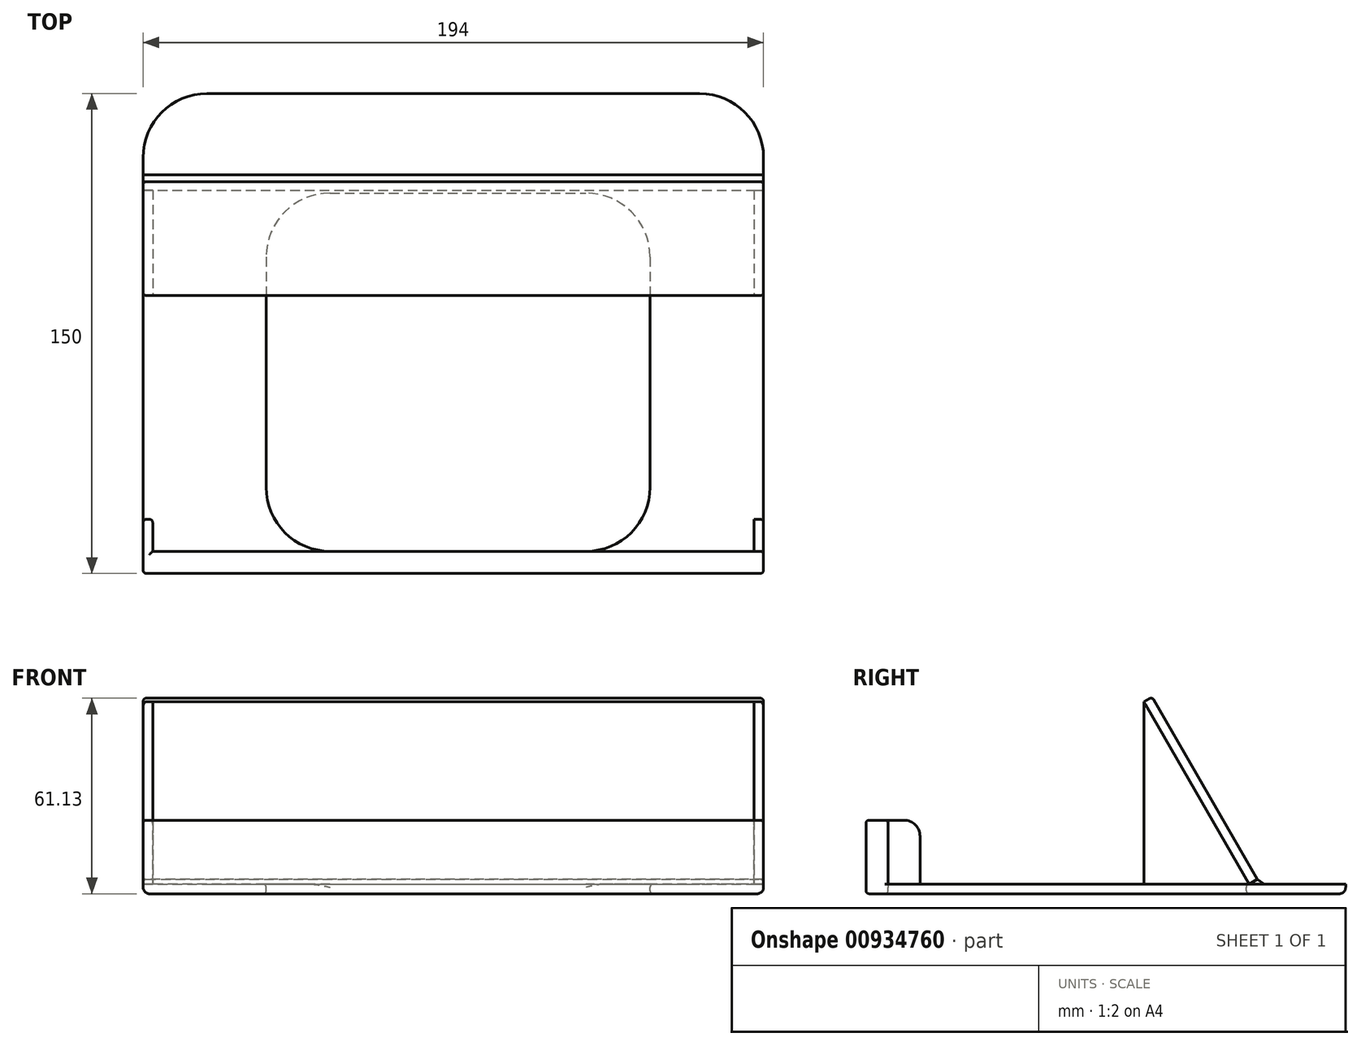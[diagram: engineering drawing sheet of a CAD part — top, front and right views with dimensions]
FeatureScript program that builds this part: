
annotation { "Feature Type Name" : "Feature", "Feature Type Description" : "" }
export const myFeature = defineFeature(function(context is Context, id is Id, definition is map)
    precondition{}
    {
        {
            var Q0;
            Q0=qCreatedBy(makeId("Top.planeOp"),FACE);
            var sketch = newSketch(context, id + "F0", { "sketchPlane" : qUnion([Q0])});
            skLineSegment(sketch, "E0.bottom", {"start": v(-88.92, 68) * mm, "end": v(105.08, 68) * mm});
            skLineSegment(sketch, "E0.top", {"start": v(-88.92, -82) * mm, "end": v(105.08, -82) * mm});
            skLineSegment(sketch, "E0.left", {"start": v(-88.92, 68) * mm, "end": v(-88.92, -82) * mm});
            skLineSegment(sketch, "E0.right", {"start": v(105.08, 68) * mm, "end": v(105.08, -82) * mm});
            skSolve(sketch);
        }
        {
            var Q0;
            Q0 = qSketchRegion(id + "F0", true);
            extrude(context, id + "F1", {"entities" : qUnion([Q0]), "depth" : 3 * mm, "offsetDistance" : 25 * mm});
        }
        {
            var Q0;
            Q0=makeQuery(id+"F1.opExtrude","SWEPT_FACE",FACE,{"disambiguationData":[OSD([sQuery(id+"F0.wireOp",EDGE,"E0.left")])]});
            var sketch = newSketch(context, id + "F2", { "sketchPlane" : qUnion([Q0])});
            skLineSegment(sketch, "E1.bottom", {"start": v(82, 3) * mm, "end": v(75.09, 3) * mm});
            skLineSegment(sketch, "E1.top", {"start": v(82, 23) * mm, "end": v(75.09, 23) * mm});
            skLineSegment(sketch, "E1.left", {"start": v(82, 3) * mm, "end": v(82, 23) * mm});
            skLineSegment(sketch, "E1.right", {"start": v(75.09, 3) * mm, "end": v(75.09, 23) * mm});
            skSolve(sketch);
        }
        {
            var Q0;
            Q0=makeQuery(id+"F2.imprint","IMPRINT",FACE,{"disambiguationData":[TD([[makeQuery(id+"F2.imprint","IMPRINT",EDGE,{"derivedFrom":sQuery(id+"F2.wireOp",EDGE,"E1.bottom")}),1.0]])]});
            extrude(context, id + "F3", {"entities" : qUnion([Q0]), "operationType" : NewBodyOperationType.ADD, "oppositeDirection" : true, "depth" : 194 * mm, "offsetDistance" : 25 * mm});
        }
        {
            var Q0;
            Q0=makeQuery(id+"F3.boolean.opBoolean","MERGE",FACE,{"derivedFrom":[makeQuery(id+"F1.opExtrude","SWEPT_FACE",FACE,{"disambiguationData":[OSD([sQuery(id+"F0.wireOp",EDGE,"E0.left")])]}),makeQuery(id+"F3.opExtrude","CAP_FACE",FACE,{"disambiguationData":[OSD([sQuery(id+"F2.wireOp",EDGE,"E1.bottom"),sQuery(id+"F2.wireOp",EDGE,"E1.top"),sQuery(id+"F2.wireOp",EDGE,"E1.left"),sQuery(id+"F2.wireOp",EDGE,"E1.right")])],"isStart":true})]});
            var sketch = newSketch(context, id + "F4", { "sketchPlane" : qUnion([Q0])});
            skLineSegment(sketch, "E2", {"start": v(-37.82, 3) * mm, "end": v(-4.91, 60) * mm});
            skLineSegment(sketch, "E3", {"start": v(-4.91, 60) * mm, "end": v(-4.91, 3) * mm});
            skLineSegment(sketch, "E4", {"start": v(-4.91, 3) * mm, "end": v(-37.82, 3) * mm});
            skSolve(sketch);
        }
        {
            var Q0;
            Q0 = qSketchRegion(id + "F4", true);
            extrude(context, id + "F5", {"entities" : qUnion([Q0]), "operationType" : NewBodyOperationType.ADD, "oppositeDirection" : true, "depth" : 3 * mm, "offsetDistance" : 25 * mm});
        }
        {
            var Q0;
            Q0=makeQuery(id+"F1.opExtrude","SWEPT_FACE",FACE,{"disambiguationData":[OSD([sQuery(id+"F0.wireOp",EDGE,"E0.right")])]});
            var sketch = newSketch(context, id + "F6", { "sketchPlane" : qUnion([Q0])});
            skLineSegment(sketch, "E5.0", {"start": v(37.82, 3) * mm, "end": v(4.91, 60) * mm});
            skPoint(sketch, "E6.0", {"position": v(4.91, 31.5) * mm});
            skLineSegment(sketch, "E7.0", {"start": v(4.91, 60) * mm, "end": v(4.91, 3) * mm});
            skLineSegment(sketch, "E8.0", {"start": v(37.82, 3) * mm, "end": v(4.91, 3) * mm});
            skSolve(sketch);
        }
        {
            var Q0;
            Q0=makeQuery(id+"F6.imprint","IMPRINT",FACE,{"disambiguationData":[TD([[makeQuery(id+"F6.imprint","IMPRINT",EDGE,{"derivedFrom":sQuery(id+"F6.wireOp",EDGE,"E5.0")}),1.0]])]});
            extrude(context, id + "F7", {"entities" : qUnion([Q0]), "oppositeDirection" : true, "depth" : 3 * mm, "offsetDistance" : 25 * mm});
        }
        {
            var Q0;
            Q0=makeQuery(id+"F7.opExtrude","SWEPT_FACE",FACE,{"disambiguationData":[OSD([sQuery(id+"F6.wireOp",EDGE,"E5.0")])]});
            var sketch = newSketch(context, id + "F8", { "sketchPlane" : qUnion([Q0])});
            skLineSegment(sketch, "E9.0", {"start": v(-105.08, -16.31) * mm, "end": v(-105.08, 49.5) * mm});
            skLineSegment(sketch, "E10.0", {"start": v(88.92, -16.31) * mm, "end": v(88.92, 49.5) * mm});
            skLineSegment(sketch, "E11", {"start": v(-105.08, 49.5) * mm, "end": v(88.92, 49.5) * mm});
            skLineSegment(sketch, "E12", {"start": v(-105.08, -16.31) * mm, "end": v(88.92, -16.31) * mm});
            skSolve(sketch);
        }
        {
            var Q0;
            Q0 = qSketchRegion(id + "F8", true);
            extrude(context, id + "F9", {"entities" : qUnion([Q0]), "depth" : 3 * mm, "offsetDistance" : 25 * mm});
        }
        {
            var Q0;
            Q0=makeQuery(id+"F9.opExtrude","SWEPT_FACE",FACE,{"disambiguationData":[OSD([sQuery(id+"F8.wireOp",EDGE,"E10.0")])]});
            var sketch = newSketch(context, id + "F10", { "sketchPlane" : qUnion([Q0])});
            skLineSegment(sketch, "E13.0", {"start": v(-40.42, 4.5) * mm, "end": v(-37.82, 3) * mm});
            skLineSegment(sketch, "E14.0", {"start": v(-68, 3) * mm, "end": v(-37.82, 3) * mm});
            skLineSegment(sketch, "E15", {"start": v(-40.42, 4.5) * mm, "end": v(-42.55, 3) * mm});
            skLineSegment(sketch, "E16", {"start": v(-42.55, 3) * mm, "end": v(-37.82, 3) * mm});
            skSolve(sketch);
        }
        {
            var Q0;
            Q0=makeQuery(id+"F10.imprint","IMPRINT",FACE,{"disambiguationData":[TD([[makeQuery(id+"F10.imprint","IMPRINT",EDGE,{"derivedFrom":sQuery(id+"F10.wireOp",EDGE,"E13.0")}),-1.0]])]});
            extrude(context, id + "F11", {"entities" : qUnion([Q0]), "oppositeDirection" : true, "depth" : 194 * mm, "offsetDistance" : 25 * mm});
        }
        {
            var Q0;
            Q0=makeQuery(id+"F5.boolean.opBoolean","MERGE",FACE,{"derivedFrom":[makeQuery(id+"F3.boolean.opBoolean","MERGE",FACE,{"derivedFrom":[makeQuery(id+"F1.opExtrude","SWEPT_FACE",FACE,{"disambiguationData":[OSD([sQuery(id+"F0.wireOp",EDGE,"E0.left")])]}),makeQuery(id+"F3.opExtrude","CAP_FACE",FACE,{"disambiguationData":[OSD([sQuery(id+"F2.wireOp",EDGE,"E1.bottom"),sQuery(id+"F2.wireOp",EDGE,"E1.top"),sQuery(id+"F2.wireOp",EDGE,"E1.left"),sQuery(id+"F2.wireOp",EDGE,"E1.right")])],"isStart":true})]}),makeQuery(id+"F5.opExtrude","CAP_FACE",FACE,{"disambiguationData":[OSD([sQuery(id+"F4.wireOp",EDGE,"E2"),sQuery(id+"F4.wireOp",EDGE,"E3"),sQuery(id+"F4.wireOp",EDGE,"E4")])],"isStart":true})]});
            var sketch = newSketch(context, id + "F12", { "sketchPlane" : qUnion([Q0])});
            skLineSegment(sketch, "E17.bottom", {"start": v(75.09, 23) * mm, "end": v(65.09, 23) * mm});
            skLineSegment(sketch, "E17.top", {"start": v(75.09, 3) * mm, "end": v(65.09, 3) * mm});
            skLineSegment(sketch, "E17.left", {"start": v(75.09, 23) * mm, "end": v(75.09, 3) * mm});
            skLineSegment(sketch, "E17.right", {"start": v(65.09, 23) * mm, "end": v(65.09, 3) * mm});
            skSolve(sketch);
        }
        {
            var Q0;
            Q0 = qSketchRegion(id + "F12", true);
            extrude(context, id + "F13", {"entities" : qUnion([Q0]), "operationType" : NewBodyOperationType.ADD, "oppositeDirection" : true, "depth" : 3 * mm, "offsetDistance" : 25 * mm});
        }
        {
            var Q0;
            Q0=makeQuery(id+"F13.opExtrude","SWEPT_EDGE",EDGE,{"disambiguationData":[OSD([sQuery(id+"F12.wireOp",EDGE,"E17.bottom"),sQuery(id+"F12.wireOp",EDGE,"E17.right")])]});
            fillet(context, id + "F14", {"entities" : qUnion([Q0]), "radius" : 5 * mm, "tangentPropagation" : true, "allowEdgeOverflow" : false});
        }
        {
            var Q0;
            Q0=makeQuery(id+"F9.opExtrude","CAP_EDGE",EDGE,{"disambiguationData":[OSD([sQuery(id+"F8.wireOp",EDGE,"E11")])],"isStart":false});
            fillet(context, id + "F15", {"entities" : qUnion([Q0]), "radius" : 1 * mm, "tangentPropagation" : true, "allowEdgeOverflow" : false});
        }
        {
            var Q0;
            Q0=makeQuery(id+"F9.opExtrude","CAP_EDGE",EDGE,{"disambiguationData":[OSD([sQuery(id+"F8.wireOp",EDGE,"E10.0")])],"isStart":false});
            fillet(context, id + "F16", {"entities" : qUnion([Q0]), "radius" : 1 * mm, "tangentPropagation" : true, "allowEdgeOverflow" : false});
        }
        {
            var Q0;
            Q0=makeQuery(id+"F3.boolean.opBoolean","MERGE",FACE,{"derivedFrom":[makeQuery(id+"F1.opExtrude","SWEPT_FACE",FACE,{"disambiguationData":[OSD([sQuery(id+"F0.wireOp",EDGE,"E0.right")])]}),makeQuery(id+"F3.opExtrude","CAP_FACE",FACE,{"disambiguationData":[OSD([sQuery(id+"F2.wireOp",EDGE,"E1.bottom"),sQuery(id+"F2.wireOp",EDGE,"E1.top"),sQuery(id+"F2.wireOp",EDGE,"E1.left"),sQuery(id+"F2.wireOp",EDGE,"E1.right")])],"isStart":false})]});
            var sketch = newSketch(context, id + "F17", { "sketchPlane" : qUnion([Q0])});
            skPoint(sketch, "E18.0", {"position": v(-72.59, 23) * mm});
            skArc(sketch, "E19.0", {"start": v(-65.09, 18) * mm, "mid": v(-66.55, 21.54) * mm, "end": v(-70.09, 23) * mm});
            skLineSegment(sketch, "E20.0", {"start": v(-65.09, 18) * mm, "end": v(-65.09, 3) * mm});
            skLineSegment(sketch, "E21.0.0", {"start": v(-65.09, 3) * mm, "end": v(-65.09, 18) * mm});
            skLineSegment(sketch, "E21.0.2", {"start": v(-70.09, 23) * mm, "end": v(-75.09, 23) * mm});
            skLineSegment(sketch, "E21.0.3", {"start": v(-75.09, 23) * mm, "end": v(-75.09, 3) * mm});
            skLineSegment(sketch, "E21.0.4", {"start": v(-75.09, 3) * mm, "end": v(-65.09, 3) * mm});
            skSolve(sketch);
        }
        {
            var Q0;
            Q0 = qSketchRegion(id + "F17", true);
            extrude(context, id + "F18", {"entities" : qUnion([Q0]), "oppositeDirection" : true, "depth" : 3 * mm, "offsetDistance" : 25 * mm});
        }
        {
            var Q0;
            Q0=makeQuery(id+"F9.opExtrude","CAP_EDGE",EDGE,{"disambiguationData":[OSD([sQuery(id+"F8.wireOp",EDGE,"E9.0")])],"isStart":false});
            fillet(context, id + "F19", {"entities" : qUnion([Q0]), "radius" : 1 * mm, "tangentPropagation" : true, "allowEdgeOverflow" : false});
        }
        {
            var Q0;
            Q0=makeQuery(id+"F7.opExtrude","CAP_EDGE",EDGE,{"disambiguationData":[OSD([sQuery(id+"F6.wireOp",EDGE,"E7.0")])],"isStart":true});
            fillet(context, id + "F20", {"entities" : qUnion([Q0]), "radius" : 1 * mm, "tangentPropagation" : true, "allowEdgeOverflow" : false});
        }
        {
            var Q0;
            Q0=makeQuery(id+"F3.opExtrude","SWEPT_EDGE",EDGE,{"disambiguationData":[OSD([sQuery(id+"F2.wireOp",EDGE,"E1.top"),sQuery(id+"F2.wireOp",EDGE,"E1.left")])]});
            fillet(context, id + "F21", {"entities" : qUnion([Q0]), "radius" : 1 * mm, "tangentPropagation" : true, "allowEdgeOverflow" : false});
        }
        {
            var Q0;
            Q0=makeQuery(id+"F1.opExtrude","CAP_FACE",FACE,{"disambiguationData":[OSD([sQuery(id+"F0.wireOp",EDGE,"E0.bottom"),sQuery(id+"F0.wireOp",EDGE,"E0.top"),sQuery(id+"F0.wireOp",EDGE,"E0.left"),sQuery(id+"F0.wireOp",EDGE,"E0.right")])],"isStart":false});
            var sketch = newSketch(context, id + "F22", { "sketchPlane" : qUnion([Q0])});
            skPoint(sketch, "E22", {"position": v(9.58, -75.09) * mm});
            skLineSegment(sketch, "E23.bottom", {"start": v(-50.42, 36.91) * mm, "end": v(69.58, 36.91) * mm});
            skLineSegment(sketch, "E23.top", {"start": v(-50.42, -75.09) * mm, "end": v(69.58, -75.09) * mm});
            skLineSegment(sketch, "E23.left", {"start": v(-50.42, 36.91) * mm, "end": v(-50.42, -75.09) * mm});
            skLineSegment(sketch, "E23.right", {"start": v(69.58, 36.91) * mm, "end": v(69.58, -75.09) * mm});
            skSolve(sketch);
        }
        {
            var Q0;
            Q0 = qSketchRegion(id + "F22", true);
            extrude(context, id + "F23", {"entities" : qUnion([Q0]), "operationType" : NewBodyOperationType.REMOVE, "endBound" : BoundingType.THROUGH_ALL, "oppositeDirection" : true, "depth" : 25 * mm, "offsetDistance" : 25 * mm});
        }
        {
            var Q0;
            Q0=makeQuery(id+"F1.opExtrude","SWEPT_EDGE",EDGE,{"disambiguationData":[OSD([sQuery(id+"F0.wireOp",EDGE,"E0.bottom"),sQuery(id+"F0.wireOp",EDGE,"E0.left")])]});
            var Q1;
            Q1=makeQuery(id+"F1.opExtrude","SWEPT_EDGE",EDGE,{"disambiguationData":[OSD([sQuery(id+"F0.wireOp",EDGE,"E0.bottom"),sQuery(id+"F0.wireOp",EDGE,"E0.right")])]});
            var Q2;
            Q2=makeQuery(id+"F23.boolean.opBoolean","COPY",EDGE,{"derivedFrom":makeQuery(id+"F23.opExtrude","SWEPT_EDGE",EDGE,{"disambiguationData":[OSD([sQuery(id+"F22.wireOp",EDGE,"E23.bottom"),sQuery(id+"F22.wireOp",EDGE,"E23.right")])]})});
            var Q3;
            Q3=makeQuery(id+"F23.boolean.opBoolean","COPY",EDGE,{"derivedFrom":makeQuery(id+"F23.opExtrude","SWEPT_EDGE",EDGE,{"disambiguationData":[OSD([sQuery(id+"F22.wireOp",EDGE,"E23.bottom"),sQuery(id+"F22.wireOp",EDGE,"E23.left")])]})});
            fillet(context, id + "F24", {"entities" : qUnion([Q0, Q1, Q2, Q3]), "radius" : 20 * mm, "tangentPropagation" : true, "allowEdgeOverflow" : false});
        }
        {
            var Q0;
            Q0=makeQuery(id+"F23.boolean.opBoolean","COPY",EDGE,{"derivedFrom":makeQuery(id+"F23.opExtrude","SWEPT_EDGE",EDGE,{"disambiguationData":[OSD([sQuery(id+"F0.wireOp",EDGE,"E0.left"),sQuery(id+"F2.wireOp",EDGE,"E1.bottom"),sQuery(id+"F2.wireOp",EDGE,"E1.right"),sQuery(id+"F22.wireOp",EDGE,"E23.top"),sQuery(id+"F22.wireOp",EDGE,"E23.right")])]})});
            var Q1;
            Q1=makeQuery(id+"F23.boolean.opBoolean","COPY",EDGE,{"derivedFrom":makeQuery(id+"F23.opExtrude","SWEPT_EDGE",EDGE,{"disambiguationData":[OSD([sQuery(id+"F0.wireOp",EDGE,"E0.left"),sQuery(id+"F2.wireOp",EDGE,"E1.bottom"),sQuery(id+"F2.wireOp",EDGE,"E1.right"),sQuery(id+"F22.wireOp",EDGE,"E23.top"),sQuery(id+"F22.wireOp",EDGE,"E23.left")])]})});
            fillet(context, id + "F25", {"entities" : qUnion([Q0, Q1]), "radius" : 20 * mm, "tangentPropagation" : true, "allowEdgeOverflow" : false});
        }
        {
            var Q0;
            Q0=makeQuery(id+"F1.opExtrude","CAP_EDGE",EDGE,{"disambiguationData":[OSD([sQuery(id+"F0.wireOp",EDGE,"E0.left")])],"isStart":true});
            fillet(context, id + "F26", {"entities" : qUnion([Q0]), "radius" : 2 * mm, "tangentPropagation" : true, "allowEdgeOverflow" : false});
        }
        {
            var Q0;
            Q0=makeQuery(id+"F5.opExtrude","CAP_EDGE",EDGE,{"disambiguationData":[OSD([sQuery(id+"F4.wireOp",EDGE,"E3")])],"isStart":true});
            fillet(context, id + "F27", {"entities" : qUnion([Q0]), "radius" : 1 * mm, "tangentPropagation" : true, "allowEdgeOverflow" : false});
        }
        {
            var Q0;
            Q0=makeQuery(id+"F3.boolean.opBoolean","MERGE",FACE,{"derivedFrom":[makeQuery(id+"F1.opExtrude","SWEPT_FACE",FACE,{"disambiguationData":[OSD([sQuery(id+"F0.wireOp",EDGE,"E0.top")])]}),makeQuery(id+"F3.opExtrude","SWEPT_FACE",FACE,{"disambiguationData":[OSD([sQuery(id+"F2.wireOp",EDGE,"E1.left")])]})]});
            fillet(context, id + "F28", {"entities" : qUnion([Q0]), "radius" : 1 * mm, "tangentPropagation" : true, "allowEdgeOverflow" : false});
        }
        {
            var Q0;
            {var subQ0=sQuery(id+"F0.wireOp",EDGE,"E0.left");Q0=makeQuery(id+"F25.opFillet","BLEND_EDGE",EDGE,{"blendedFrom":[makeQuery(id+"F23.boolean.opBoolean","COPY",EDGE,{"derivedFrom":makeQuery(id+"F23.opExtrude","SWEPT_EDGE",EDGE,{"disambiguationData":[OSD([subQ0,sQuery(id+"F2.wireOp",EDGE,"E1.bottom"),sQuery(id+"F2.wireOp",EDGE,"E1.right"),sQuery(id+"F22.wireOp",EDGE,"E23.top"),sQuery(id+"F22.wireOp",EDGE,"E23.left")])]})}),makeQuery(id+"F1.opExtrude","CAP_FACE",FACE,{"disambiguationData":[OSD([sQuery(id+"F0.wireOp",EDGE,"E0.bottom"),sQuery(id+"F0.wireOp",EDGE,"E0.top"),subQ0,sQuery(id+"F0.wireOp",EDGE,"E0.right")])],"isStart":true})],"blendedInto":[makeQuery(id+"F1.opExtrude","CAP_FACE",FACE,{"disambiguationData":[OSD([sQuery(id+"F0.wireOp",EDGE,"E0.bottom"),sQuery(id+"F0.wireOp",EDGE,"E0.top"),subQ0,sQuery(id+"F0.wireOp",EDGE,"E0.right")])],"isStart":true})]});}
            var Q1;
            {var subQ0=sQuery(id+"F0.wireOp",EDGE,"E0.left");Q1=makeQuery(id+"F25.opFillet","BLEND_EDGE",EDGE,{"blendedFrom":[makeQuery(id+"F23.boolean.opBoolean","COPY",EDGE,{"derivedFrom":makeQuery(id+"F23.opExtrude","SWEPT_EDGE",EDGE,{"disambiguationData":[OSD([subQ0,sQuery(id+"F2.wireOp",EDGE,"E1.bottom"),sQuery(id+"F2.wireOp",EDGE,"E1.right"),sQuery(id+"F22.wireOp",EDGE,"E23.top"),sQuery(id+"F22.wireOp",EDGE,"E23.right")])]})}),makeQuery(id+"F1.opExtrude","CAP_FACE",FACE,{"disambiguationData":[OSD([sQuery(id+"F0.wireOp",EDGE,"E0.bottom"),sQuery(id+"F0.wireOp",EDGE,"E0.top"),subQ0,sQuery(id+"F0.wireOp",EDGE,"E0.right")])],"isStart":true})],"blendedInto":[makeQuery(id+"F1.opExtrude","CAP_FACE",FACE,{"disambiguationData":[OSD([sQuery(id+"F0.wireOp",EDGE,"E0.bottom"),sQuery(id+"F0.wireOp",EDGE,"E0.top"),subQ0,sQuery(id+"F0.wireOp",EDGE,"E0.right")])],"isStart":true})]});}
            var Q2;
            Q2=makeQuery(id+"F23.boolean.opBoolean","INTERSECT",EDGE,{"derivedFrom":[makeQuery(id+"F1.opExtrude","CAP_FACE",FACE,{"disambiguationData":[OSD([sQuery(id+"F0.wireOp",EDGE,"E0.bottom"),sQuery(id+"F0.wireOp",EDGE,"E0.top"),sQuery(id+"F0.wireOp",EDGE,"E0.left"),sQuery(id+"F0.wireOp",EDGE,"E0.right")])],"isStart":true}),makeQuery(id+"F23.opExtrude","SWEPT_FACE",FACE,{"disambiguationData":[OSD([sQuery(id+"F22.wireOp",EDGE,"E23.top")])]})]});
            var Q3;
            Q3=makeQuery(id+"F24.opFillet","BLEND_EDGE",EDGE,{"blendedFrom":[makeQuery(id+"F23.boolean.opBoolean","COPY",EDGE,{"derivedFrom":makeQuery(id+"F23.opExtrude","SWEPT_EDGE",EDGE,{"disambiguationData":[OSD([sQuery(id+"F22.wireOp",EDGE,"E23.bottom"),sQuery(id+"F22.wireOp",EDGE,"E23.right")])]})}),makeQuery(id+"F1.opExtrude","CAP_FACE",FACE,{"disambiguationData":[OSD([sQuery(id+"F0.wireOp",EDGE,"E0.bottom"),sQuery(id+"F0.wireOp",EDGE,"E0.top"),sQuery(id+"F0.wireOp",EDGE,"E0.left"),sQuery(id+"F0.wireOp",EDGE,"E0.right")])],"isStart":true})],"blendedInto":[makeQuery(id+"F1.opExtrude","CAP_FACE",FACE,{"disambiguationData":[OSD([sQuery(id+"F0.wireOp",EDGE,"E0.bottom"),sQuery(id+"F0.wireOp",EDGE,"E0.top"),sQuery(id+"F0.wireOp",EDGE,"E0.left"),sQuery(id+"F0.wireOp",EDGE,"E0.right")])],"isStart":true})]});
            var Q4;
            Q4=makeQuery(id+"F23.boolean.opBoolean","INTERSECT",EDGE,{"derivedFrom":[makeQuery(id+"F1.opExtrude","CAP_FACE",FACE,{"disambiguationData":[OSD([sQuery(id+"F0.wireOp",EDGE,"E0.bottom"),sQuery(id+"F0.wireOp",EDGE,"E0.top"),sQuery(id+"F0.wireOp",EDGE,"E0.left"),sQuery(id+"F0.wireOp",EDGE,"E0.right")])],"isStart":true}),makeQuery(id+"F23.opExtrude","SWEPT_FACE",FACE,{"disambiguationData":[OSD([sQuery(id+"F22.wireOp",EDGE,"E23.right")])]})]});
            var Q5;
            Q5=makeQuery(id+"F23.boolean.opBoolean","INTERSECT",EDGE,{"derivedFrom":[makeQuery(id+"F1.opExtrude","CAP_FACE",FACE,{"disambiguationData":[OSD([sQuery(id+"F0.wireOp",EDGE,"E0.bottom"),sQuery(id+"F0.wireOp",EDGE,"E0.top"),sQuery(id+"F0.wireOp",EDGE,"E0.left"),sQuery(id+"F0.wireOp",EDGE,"E0.right")])],"isStart":true}),makeQuery(id+"F23.opExtrude","SWEPT_FACE",FACE,{"disambiguationData":[OSD([sQuery(id+"F22.wireOp",EDGE,"E23.bottom")])]})]});
            var Q6;
            Q6=makeQuery(id+"F24.opFillet","BLEND_EDGE",EDGE,{"blendedFrom":[makeQuery(id+"F23.boolean.opBoolean","COPY",EDGE,{"derivedFrom":makeQuery(id+"F23.opExtrude","SWEPT_EDGE",EDGE,{"disambiguationData":[OSD([sQuery(id+"F22.wireOp",EDGE,"E23.bottom"),sQuery(id+"F22.wireOp",EDGE,"E23.left")])]})}),makeQuery(id+"F1.opExtrude","CAP_FACE",FACE,{"disambiguationData":[OSD([sQuery(id+"F0.wireOp",EDGE,"E0.bottom"),sQuery(id+"F0.wireOp",EDGE,"E0.top"),sQuery(id+"F0.wireOp",EDGE,"E0.left"),sQuery(id+"F0.wireOp",EDGE,"E0.right")])],"isStart":true})],"blendedInto":[makeQuery(id+"F1.opExtrude","CAP_FACE",FACE,{"disambiguationData":[OSD([sQuery(id+"F0.wireOp",EDGE,"E0.bottom"),sQuery(id+"F0.wireOp",EDGE,"E0.top"),sQuery(id+"F0.wireOp",EDGE,"E0.left"),sQuery(id+"F0.wireOp",EDGE,"E0.right")])],"isStart":true})]});
            var Q7;
            Q7=makeQuery(id+"F23.boolean.opBoolean","INTERSECT",EDGE,{"derivedFrom":[makeQuery(id+"F1.opExtrude","CAP_FACE",FACE,{"disambiguationData":[OSD([sQuery(id+"F0.wireOp",EDGE,"E0.bottom"),sQuery(id+"F0.wireOp",EDGE,"E0.top"),sQuery(id+"F0.wireOp",EDGE,"E0.left"),sQuery(id+"F0.wireOp",EDGE,"E0.right")])],"isStart":true}),makeQuery(id+"F23.opExtrude","SWEPT_FACE",FACE,{"disambiguationData":[OSD([sQuery(id+"F22.wireOp",EDGE,"E23.left")])]})]});
            fillet(context, id + "F29", {"entities" : qUnion([Q0, Q1, Q2, Q3, Q4, Q5, Q6, Q7]), "radius" : 1 * mm, "tangentPropagation" : true, "allowEdgeOverflow" : false});
        }
        {
            var Q0;
            Q0=makeQuery(id+"F24.opFillet","BLEND_EDGE",EDGE,{"blendedFrom":[makeQuery(id+"F23.boolean.opBoolean","COPY",EDGE,{"derivedFrom":makeQuery(id+"F23.opExtrude","SWEPT_EDGE",EDGE,{"disambiguationData":[OSD([sQuery(id+"F22.wireOp",EDGE,"E23.bottom"),sQuery(id+"F22.wireOp",EDGE,"E23.left")])]})}),makeQuery(id+"F1.opExtrude","CAP_FACE",FACE,{"disambiguationData":[OSD([sQuery(id+"F0.wireOp",EDGE,"E0.bottom"),sQuery(id+"F0.wireOp",EDGE,"E0.top"),sQuery(id+"F0.wireOp",EDGE,"E0.left"),sQuery(id+"F0.wireOp",EDGE,"E0.right")])],"isStart":false})],"blendedInto":[makeQuery(id+"F1.opExtrude","CAP_FACE",FACE,{"disambiguationData":[OSD([sQuery(id+"F0.wireOp",EDGE,"E0.bottom"),sQuery(id+"F0.wireOp",EDGE,"E0.top"),sQuery(id+"F0.wireOp",EDGE,"E0.left"),sQuery(id+"F0.wireOp",EDGE,"E0.right")])],"isStart":false})]});
            var Q1;
            Q1=makeQuery(id+"F23.boolean.opBoolean","COPY",EDGE,{"derivedFrom":makeQuery(id+"F23.opExtrude","CAP_EDGE",EDGE,{"disambiguationData":[OSD([sQuery(id+"F22.wireOp",EDGE,"E23.left")])],"isStart":true})});
            var Q2;
            Q2=makeQuery(id+"F24.opFillet","BLEND_EDGE",EDGE,{"blendedFrom":[makeQuery(id+"F23.boolean.opBoolean","COPY",EDGE,{"derivedFrom":makeQuery(id+"F23.opExtrude","SWEPT_EDGE",EDGE,{"disambiguationData":[OSD([sQuery(id+"F22.wireOp",EDGE,"E23.bottom"),sQuery(id+"F22.wireOp",EDGE,"E23.right")])]})}),makeQuery(id+"F1.opExtrude","CAP_FACE",FACE,{"disambiguationData":[OSD([sQuery(id+"F0.wireOp",EDGE,"E0.bottom"),sQuery(id+"F0.wireOp",EDGE,"E0.top"),sQuery(id+"F0.wireOp",EDGE,"E0.left"),sQuery(id+"F0.wireOp",EDGE,"E0.right")])],"isStart":false})],"blendedInto":[makeQuery(id+"F1.opExtrude","CAP_FACE",FACE,{"disambiguationData":[OSD([sQuery(id+"F0.wireOp",EDGE,"E0.bottom"),sQuery(id+"F0.wireOp",EDGE,"E0.top"),sQuery(id+"F0.wireOp",EDGE,"E0.left"),sQuery(id+"F0.wireOp",EDGE,"E0.right")])],"isStart":false})]});
            var Q3;
            Q3=makeQuery(id+"F23.boolean.opBoolean","COPY",EDGE,{"derivedFrom":makeQuery(id+"F23.opExtrude","CAP_EDGE",EDGE,{"disambiguationData":[OSD([sQuery(id+"F22.wireOp",EDGE,"E23.right")])],"isStart":true})});
            var Q4;
            {var subQ0=sQuery(id+"F0.wireOp",EDGE,"E0.left");Q4=makeQuery(id+"F25.opFillet","BLEND_EDGE",EDGE,{"blendedFrom":[makeQuery(id+"F23.boolean.opBoolean","COPY",EDGE,{"derivedFrom":makeQuery(id+"F23.opExtrude","SWEPT_EDGE",EDGE,{"disambiguationData":[OSD([subQ0,sQuery(id+"F2.wireOp",EDGE,"E1.bottom"),sQuery(id+"F2.wireOp",EDGE,"E1.right"),sQuery(id+"F22.wireOp",EDGE,"E23.top"),sQuery(id+"F22.wireOp",EDGE,"E23.right")])]})}),makeQuery(id+"F1.opExtrude","CAP_FACE",FACE,{"disambiguationData":[OSD([sQuery(id+"F0.wireOp",EDGE,"E0.bottom"),sQuery(id+"F0.wireOp",EDGE,"E0.top"),subQ0,sQuery(id+"F0.wireOp",EDGE,"E0.right")])],"isStart":false})],"blendedInto":[makeQuery(id+"F1.opExtrude","CAP_FACE",FACE,{"disambiguationData":[OSD([sQuery(id+"F0.wireOp",EDGE,"E0.bottom"),sQuery(id+"F0.wireOp",EDGE,"E0.top"),subQ0,sQuery(id+"F0.wireOp",EDGE,"E0.right")])],"isStart":false})]});}
            var Q5;
            {var subQ0=sQuery(id+"F0.wireOp",EDGE,"E0.left");Q5=makeQuery(id+"F25.opFillet","BLEND_EDGE",EDGE,{"blendedFrom":[makeQuery(id+"F23.boolean.opBoolean","COPY",EDGE,{"derivedFrom":makeQuery(id+"F23.opExtrude","SWEPT_EDGE",EDGE,{"disambiguationData":[OSD([subQ0,sQuery(id+"F2.wireOp",EDGE,"E1.bottom"),sQuery(id+"F2.wireOp",EDGE,"E1.right"),sQuery(id+"F22.wireOp",EDGE,"E23.top"),sQuery(id+"F22.wireOp",EDGE,"E23.left")])]})}),makeQuery(id+"F1.opExtrude","CAP_FACE",FACE,{"disambiguationData":[OSD([sQuery(id+"F0.wireOp",EDGE,"E0.bottom"),sQuery(id+"F0.wireOp",EDGE,"E0.top"),subQ0,sQuery(id+"F0.wireOp",EDGE,"E0.right")])],"isStart":false})],"blendedInto":[makeQuery(id+"F1.opExtrude","CAP_FACE",FACE,{"disambiguationData":[OSD([sQuery(id+"F0.wireOp",EDGE,"E0.bottom"),sQuery(id+"F0.wireOp",EDGE,"E0.top"),subQ0,sQuery(id+"F0.wireOp",EDGE,"E0.right")])],"isStart":false})]});}
            fillet(context, id + "F30", {"entities" : qUnion([Q0, Q1, Q2, Q3, Q4, Q5]), "radius" : 1 * mm, "tangentPropagation" : true, "allowEdgeOverflow" : false});
        }
        {
            var Q0;
            Q0=makeQuery(id+"F18.opExtrude","CAP_EDGE",EDGE,{"disambiguationData":[OSD([sQuery(id+"F17.wireOp",EDGE,"E21.0.0")])],"isStart":true});
            var Q1;
            Q1=makeQuery(id+"F18.opExtrude","CAP_EDGE",EDGE,{"disambiguationData":[OSD([sQuery(id+"F17.wireOp",EDGE,"E19.0")])],"isStart":true});
            var Q2;
            Q2=makeQuery(id+"F18.opExtrude","CAP_EDGE",EDGE,{"disambiguationData":[OSD([sQuery(id+"F17.wireOp",EDGE,"E21.0.0")])],"isStart":false});
            var Q3;
            Q3=makeQuery(id+"F13.opExtrude","CAP_EDGE",EDGE,{"disambiguationData":[OSD([sQuery(id+"F12.wireOp",EDGE,"E17.right")])],"isStart":false});
            var Q4;
            Q4=makeQuery(id+"F3.opExtrude","SWEPT_EDGE",EDGE,{"disambiguationData":[OSD([sQuery(id+"F2.wireOp",EDGE,"E1.top"),sQuery(id+"F2.wireOp",EDGE,"E1.right")])]});
            fillet(context, id + "F31", {"entities" : qUnion([Q0, Q1, Q2, Q3, Q4]), "radius" : 1 * mm, "tangentPropagation" : true, "allowEdgeOverflow" : false});
        }
    });
